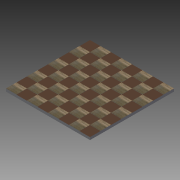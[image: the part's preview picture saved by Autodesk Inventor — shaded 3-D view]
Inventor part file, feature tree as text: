
AUTODESK INVENTOR PART (.ipt)
format: ipt  version: 2015 SP1 (Build 190203100, 203)  size: 334,848 bytes
history: native  units: mm
features: extrude x2, sketch x2
ambient origin geometry x8: Origin, YZ Plane, XZ Plane, XY Plane, X Axis, Y Axis, Z Axis, Center Point
bodies: Solid1 (feature_tree)
feature tree (4):
  extrude  "Extrusion1"  Depth=360.0mm
  extrude  "Extrusion2"  Depth=45.0mm
  sketch  "Sketch1"  dims[d0=360.0mm d1=360.0mm]
  sketch  "Sketch2"  dims[d2=45.0mm d3=45.0mm d4=80.0mm d6=45.0mm d7=80.0mm d9=45.0mm d12=11.0mm d13=0.0mm d14=45.0mm d15=45.0mm d16=40.0mm d18=90.0mm d19=40.0mm d21=90.0mm d25=40.0mm d27=40.0mm d28=45.0mm d29=45.0mm d30=90.0mm d31=90.0mm d32=0.5mm d33=0.0mm]
